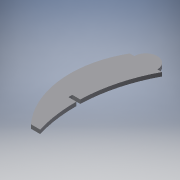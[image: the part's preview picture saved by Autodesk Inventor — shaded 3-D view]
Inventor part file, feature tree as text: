
AUTODESK INVENTOR PART (.ipt)
format: ipt  version: 2017 (Build 210142000, 142)  size: 118,272 bytes
history: native  units: mm
features: extrude x2, sketch x2, projected_geometry x1
ambient origin geometry x8: Origin, YZ Plane, XZ Plane, XY Plane, X Axis, Y Axis, Z Axis, Center Point
bodies: Solid1 (feature_tree)
feature tree (5):
  extrude  "Extrusion1"  Depth=12.7mm
  extrude  "Extrusion2"  Depth=5.3mm TaperAngle=0.0deg
  sketch  "Sketch1"  dims[d0=31.75mm d1=12.7mm]
  sketch  "Sketch2"  dims[d2=152.4mm d3=5.3mm d4=0.0mm d5=5.3mm d6=88.9mm d7=3.81mm d8=0.0mm d9=70.0mm d10=10.7mm]
  projected_geometry  "Projected Loop1"
